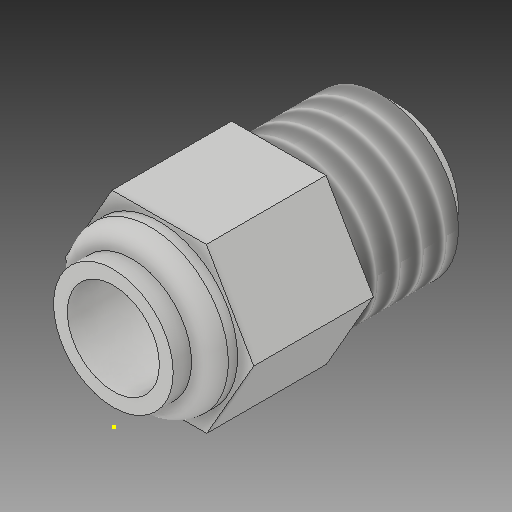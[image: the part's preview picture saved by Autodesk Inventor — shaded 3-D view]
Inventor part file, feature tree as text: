
AUTODESK INVENTOR PART (.ipt)
format: ipt  version: 2018 (Build 220112000, 112)  size: 182,272 bytes
history: native  units: mm
features: sketch x6, other x3
ambient origin geometry x8: Origin, YZ Plane, XZ Plane, XY Plane, X Axis, Y Axis, Z Axis, Center Point
bodies: Solid1 (feature_tree)
feature tree (9):
  other  "Pushfit-Adapter_MIR.ipt"
  other  "Solid1::Pushfit-Adapter_MIR.ipt"
  other  "TaggingFeature1"
  sketch  "Sketch1"  dims[d0=10.0mm]
  sketch  "Sketch2"
  sketch  "Sketch3"
  sketch  "Sketch4"
  sketch  "Sketch5"
  sketch  "Sketch6"
